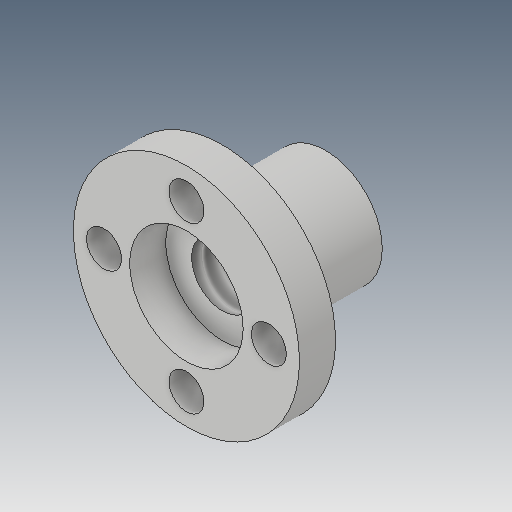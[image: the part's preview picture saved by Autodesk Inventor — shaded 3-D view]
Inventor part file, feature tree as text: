
AUTODESK INVENTOR PART (.ipt)
format: ipt  version: 2017 (Build 210142000, 142)  size: 141,312 bytes
history: native  units: mm
features: other x3, sketch x3
ambient origin geometry x8: Origin, YZ Plane, XZ Plane, XY Plane, X Axis, Y Axis, Z Axis, Center Point
bodies: Solid1 (feature_tree)
feature tree (6):
  other  "Brass-Nut.ipt"
  other  "Solid1::Brass-Nut.ipt"
  other  "TaggingFeature1"
  sketch  "Sketch1"  dims[d0=10.0mm]
  sketch  "Sketch2"
  sketch  "Sketch3"
